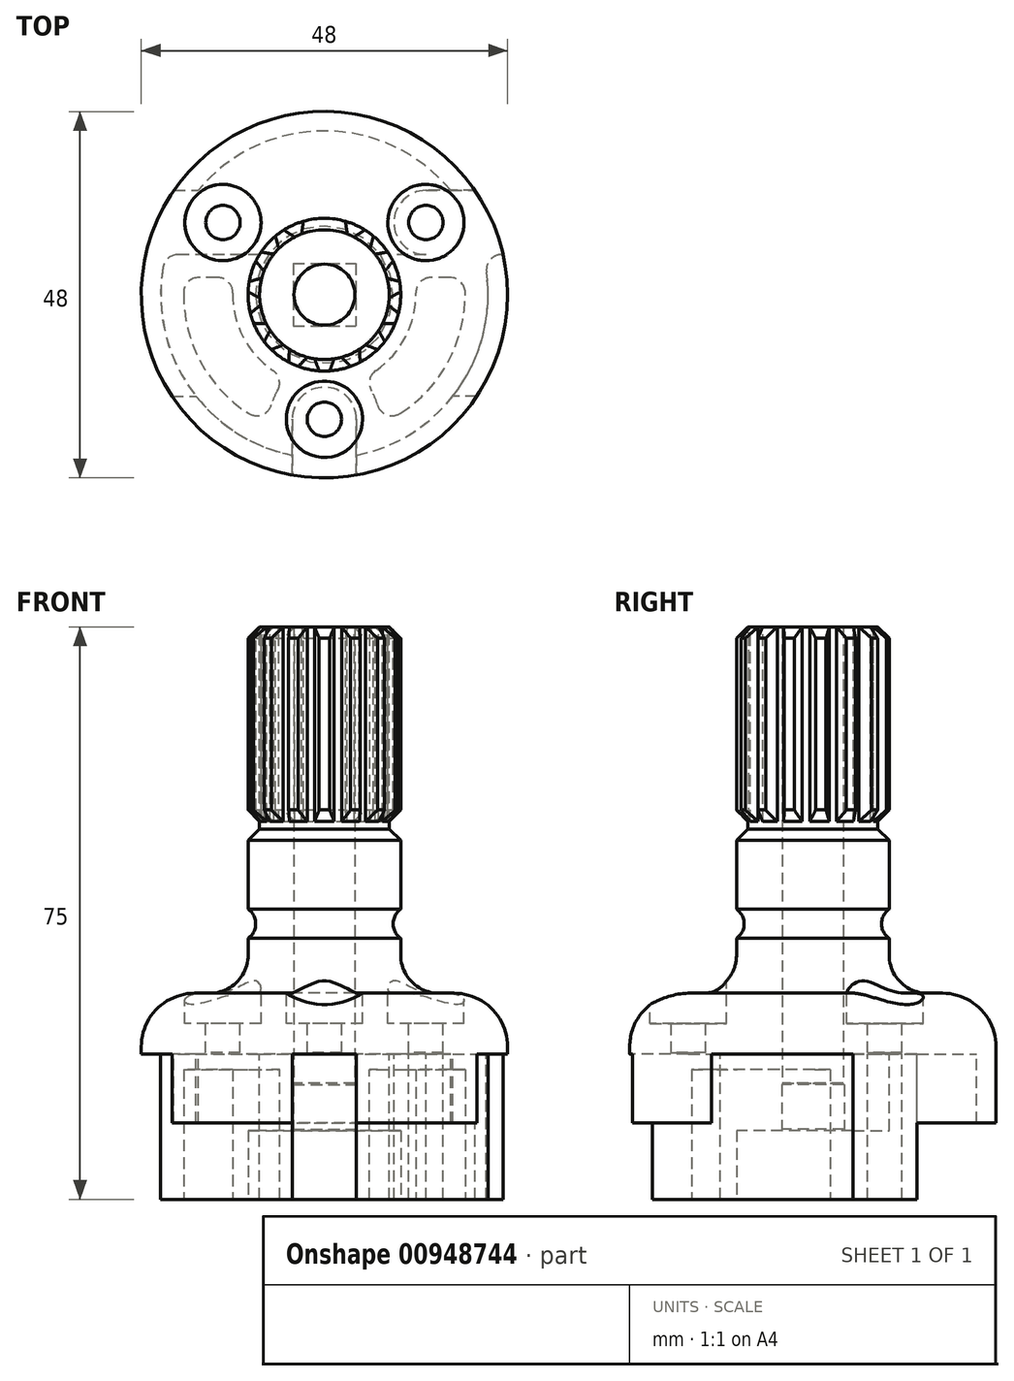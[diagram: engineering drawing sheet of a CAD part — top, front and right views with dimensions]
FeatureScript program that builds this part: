
annotation { "Feature Type Name" : "Feature", "Feature Type Description" : "" }
export const myFeature = defineFeature(function(context is Context, id is Id, definition is map)
    precondition{}
    {
        {
            var Q0;
            Q0=qCreatedBy(makeId("Front.planeOp"),FACE);
            var sketch = newSketch(context, id + "F0", { "sketchPlane" : qUnion([Q0])});
            skLineSegment(sketch, "E0", {"start": v(0, 0) * mm, "end": v(0, 75) * mm});
            skLineSegment(sketch, "E1", {"start": v(24, 0) * mm, "end": v(24, 27) * mm});
            skLineSegment(sketch, "E2", {"start": v(24, 27) * mm, "end": v(10, 27) * mm});
            skLineSegment(sketch, "E3", {"start": v(10, 27) * mm, "end": v(10, 34.2) * mm});
            skLineSegment(sketch, "E4", {"start": v(8.5, 75) * mm, "end": v(0, 75) * mm});
            skArc(sketch, "E5", {"start": v(10, 38) * mm, "mid": v(9, 36.1) * mm, "end": v(10, 34.2) * mm});
            skPoint(sketch, "E6", {"position": v(9, 36.1) * mm});
            skLineSegment(sketch, "E7.trimOffspring", {"start": v(10, 38) * mm, "end": v(10, 47) * mm});
            skLineSegment(sketch, "E8", {"start": v(10, 47) * mm, "end": v(8.5, 48.5) * mm});
            skLineSegment(sketch, "E9", {"start": v(8.5, 48.5) * mm, "end": v(8.5, 49.5) * mm});
            skLineSegment(sketch, "E10", {"start": v(8.5, 49.5) * mm, "end": v(10, 51) * mm});
            skLineSegment(sketch, "E11", {"start": v(8.5, 75) * mm, "end": v(10, 73.5) * mm});
            skPoint(sketch, "E12.orphan", {"position": v(10, 75) * mm});
            skLineSegment(sketch, "E13.trimOffspring", {"start": v(10, 51) * mm, "end": v(10, 73.5) * mm});
            skLineSegment(sketch, "E14", {"start": v(0, 0) * mm, "end": v(24, 0) * mm});
            skSolve(sketch);
        }
        {
            var Q0;
            Q0=makeQuery(id+"F0.imprint","IMPRINT",FACE,{"disambiguationData":[TD([[makeQuery(id+"F0.imprint","IMPRINT",EDGE,{"derivedFrom":sQuery(id+"F0.wireOp",EDGE,"E0")}),-1.0]])]});
            var Q1;
            Q1=sQuery(id+"F0.wireOp",EDGE,"E0");
            revolve(context, id + "F1", {"surfaceOperationType" : NewSurfaceOperationType.NEW, "entities" : qUnion([Q0]), "axis" : qUnion([Q1]), "revolveType" : RevolveType.FULL});
        }
        {
            var Q0;
            Q0=makeQuery(id+"F1.opRevolve","SWEPT_FACE",FACE,{"disambiguationData":[OSD([sQuery(id+"F0.wireOp",EDGE,"E4")])]});
            var sketch = newSketch(context, id + "F2", { "sketchPlane" : qUnion([Q0])});
            skArc(sketch, "E15.0", {"start": v(-4.59, -7.16) * mm, "mid": v(-5, -6.88) * mm, "end": v(-5.39, -6.57) * mm});
            skArc(sketch, "E15.1", {"start": v(4.69, -8.83) * mm, "mid": v(5.88, -8.1) * mm, "end": v(6.95, -7.19) * mm});
            skLineSegment(sketch, "E16", {"start": v(0, 0) * mm, "end": v(0, -10) * mm, "construction": true});
            skLineSegment(sketch, "E17", {"start": v(0.7, -9.98) * mm, "end": v(1.28, -8.4) * mm});
            skLineSegment(sketch, "E18.MirrorCS", {"start": v(-0.7, -9.98) * mm, "end": v(-1.28, -8.4) * mm});
            skLineSegment(sketch, "E19.1.0", {"start": v(4.69, -8.83) * mm, "end": v(4.59, -7.16) * mm});
            skLineSegment(sketch, "E19.1.1", {"start": v(3.43, -9.4) * mm, "end": v(2.25, -8.2) * mm});
            skLineSegment(sketch, "E19.2.0", {"start": v(7.88, -6.16) * mm, "end": v(7.1, -4.67) * mm});
            skLineSegment(sketch, "E19.2.1", {"start": v(6.95, -7.19) * mm, "end": v(5.39, -6.57) * mm});
            skLineSegment(sketch, "E19.3.0", {"start": v(9.7, -2.43) * mm, "end": v(8.39, -1.38) * mm});
            skLineSegment(sketch, "E19.3.1", {"start": v(9.27, -3.74) * mm, "end": v(7.6, -3.81) * mm});
            skLineSegment(sketch, "E19.4.0", {"start": v(9.85, 1.73) * mm, "end": v(8.22, 2.15) * mm});
            skLineSegment(sketch, "E19.4.1", {"start": v(10, 0.36) * mm, "end": v(8.5, -0.4) * mm});
            skLineSegment(sketch, "E19.5.0", {"start": v(8.3, 5.59) * mm, "end": v(6.64, 5.31) * mm});
            skLineSegment(sketch, "E19.5.1", {"start": v(8.99, 4.39) * mm, "end": v(7.92, 3.1) * mm});
            skLineSegment(sketch, "E19.6.0", {"start": v(5.3, 8.48) * mm, "end": v(3.9, 7.55) * mm});
            skLineSegment(sketch, "E19.6.1", {"start": v(6.42, 7.66) * mm, "end": v(5.98, 6.05) * mm});
            skLineSegment(sketch, "E19.7.1", {"start": v(2.75, 9.61) * mm, "end": v(3, 7.95) * mm});
            skLineSegment(sketch, "E19.8.0", {"start": v(-2.75, 9.61) * mm, "end": v(-3, 7.95) * mm});
            skLineSegment(sketch, "E19.9.0", {"start": v(-6.42, 7.66) * mm, "end": v(-5.98, 6.05) * mm});
            skLineSegment(sketch, "E19.9.1", {"start": v(-5.3, 8.48) * mm, "end": v(-3.9, 7.55) * mm});
            skLineSegment(sketch, "E19.10.0", {"start": v(-8.99, 4.39) * mm, "end": v(-7.92, 3.1) * mm});
            skLineSegment(sketch, "E19.10.1", {"start": v(-8.3, 5.59) * mm, "end": v(-6.64, 5.31) * mm});
            skLineSegment(sketch, "E19.11.0", {"start": v(-10, 0.36) * mm, "end": v(-8.5, -0.4) * mm});
            skLineSegment(sketch, "E19.11.1", {"start": v(-9.85, 1.73) * mm, "end": v(-8.22, 2.15) * mm});
            skLineSegment(sketch, "E19.12.0", {"start": v(-9.27, -3.74) * mm, "end": v(-7.6, -3.81) * mm});
            skLineSegment(sketch, "E19.12.1", {"start": v(-9.7, -2.43) * mm, "end": v(-8.39, -1.38) * mm});
            skLineSegment(sketch, "E19.13.0", {"start": v(-6.95, -7.19) * mm, "end": v(-5.39, -6.57) * mm});
            skLineSegment(sketch, "E19.13.1", {"start": v(-7.88, -6.16) * mm, "end": v(-7.1, -4.67) * mm});
            skLineSegment(sketch, "E19.14.0", {"start": v(-3.43, -9.4) * mm, "end": v(-2.25, -8.2) * mm});
            skLineSegment(sketch, "E19.14.1", {"start": v(-4.69, -8.83) * mm, "end": v(-4.59, -7.16) * mm});
            skArc(sketch, "E20.trimOffspring", {"start": v(-7.1, -4.67) * mm, "mid": v(-7.36, -4.25) * mm, "end": v(-7.6, -3.81) * mm});
            skArc(sketch, "E21.trimOffspring", {"start": v(-8.39, -1.38) * mm, "mid": v(-8.45, -0.89) * mm, "end": v(-8.5, -0.4) * mm});
            skArc(sketch, "E22.trimOffspring", {"start": v(-8.22, 2.15) * mm, "mid": v(-8.08, 2.63) * mm, "end": v(-7.92, 3.1) * mm});
            skArc(sketch, "E23.trimOffspring", {"start": v(-6.64, 5.31) * mm, "mid": v(-6.32, 5.69) * mm, "end": v(-5.98, 6.05) * mm});
            skArc(sketch, "E24.trimOffspring", {"start": v(-3.9, 7.55) * mm, "mid": v(-3.46, 7.77) * mm, "end": v(-3, 7.95) * mm});
            skArc(sketch, "E25.trimOffspring", {"start": v(3, 7.95) * mm, "mid": v(3.46, 7.77) * mm, "end": v(3.9, 7.55) * mm});
            skArc(sketch, "E26.trimOffspring", {"start": v(5.98, 6.05) * mm, "mid": v(6.32, 5.69) * mm, "end": v(6.64, 5.31) * mm});
            skArc(sketch, "E27.trimOffspring", {"start": v(7.92, 3.1) * mm, "mid": v(8.08, 2.63) * mm, "end": v(8.22, 2.15) * mm});
            skArc(sketch, "E28.trimOffspring", {"start": v(8.5, -0.4) * mm, "mid": v(8.45, -0.89) * mm, "end": v(8.39, -1.38) * mm});
            skArc(sketch, "E29.trimOffspring", {"start": v(7.6, -3.81) * mm, "mid": v(7.36, -4.25) * mm, "end": v(7.1, -4.67) * mm});
            skArc(sketch, "E30.trimOffspring", {"start": v(5.39, -6.57) * mm, "mid": v(5, -6.88) * mm, "end": v(4.59, -7.16) * mm});
            skArc(sketch, "E31.trimOffspring", {"start": v(2.25, -8.2) * mm, "mid": v(1.77, -8.31) * mm, "end": v(1.28, -8.4) * mm});
            skArc(sketch, "E32.trimOffspring", {"start": v(-1.28, -8.4) * mm, "mid": v(-1.77, -8.31) * mm, "end": v(-2.25, -8.2) * mm});
            skArc(sketch, "E33.trimOffspring", {"start": v(7.88, -6.16) * mm, "mid": v(8.66, -5) * mm, "end": v(9.27, -3.74) * mm});
            skArc(sketch, "E34.trimOffspring", {"start": v(9.7, -2.43) * mm, "mid": v(9.95, -1.05) * mm, "end": v(10, 0.36) * mm});
            skArc(sketch, "E35.trimOffspring", {"start": v(9.85, 1.73) * mm, "mid": v(9.51, 3.1) * mm, "end": v(8.99, 4.39) * mm});
            skArc(sketch, "E36.trimOffspring", {"start": v(8.3, 5.59) * mm, "mid": v(7.43, 6.7) * mm, "end": v(6.42, 7.66) * mm});
            skArc(sketch, "E37.trimOffspring", {"start": v(5.3, 8.48) * mm, "mid": v(4.07, 9.14) * mm, "end": v(2.75, 9.61) * mm});
            skArc(sketch, "E38.trimOffspring", {"start": v(-2.75, 9.61) * mm, "mid": v(-4.07, 9.14) * mm, "end": v(-5.3, 8.48) * mm});
            skArc(sketch, "E39.trimOffspring", {"start": v(-6.42, 7.66) * mm, "mid": v(-7.43, 6.7) * mm, "end": v(-8.3, 5.59) * mm});
            skArc(sketch, "E40.trimOffspring", {"start": v(-8.99, 4.39) * mm, "mid": v(-9.51, 3.1) * mm, "end": v(-9.85, 1.73) * mm});
            skArc(sketch, "E41.trimOffspring", {"start": v(-10, 0.36) * mm, "mid": v(-9.95, -1.05) * mm, "end": v(-9.7, -2.43) * mm});
            skArc(sketch, "E42.trimOffspring", {"start": v(-9.27, -3.74) * mm, "mid": v(-8.66, -5) * mm, "end": v(-7.88, -6.16) * mm});
            skArc(sketch, "E43.trimOffspring", {"start": v(-6.95, -7.19) * mm, "mid": v(-5.88, -8.1) * mm, "end": v(-4.69, -8.83) * mm});
            skArc(sketch, "E44.trimOffspring", {"start": v(-3.43, -9.4) * mm, "mid": v(-2.08, -9.78) * mm, "end": v(-0.7, -9.98) * mm});
            skArc(sketch, "E45.trimOffspring", {"start": v(0.7, -9.98) * mm, "mid": v(2.08, -9.78) * mm, "end": v(3.43, -9.4) * mm});
            skLineSegment(sketch, "E46", {"start": v(0, 0) * mm, "end": v(2.08, -9.78) * mm, "construction": true});
            skSolve(sketch);
        }
        {
            var Q0;
            Q0 = qSketchRegion(id + "F2", true);
            extrude(context, id + "F3", {"entities" : qUnion([Q0]), "operationType" : NewBodyOperationType.REMOVE, "oppositeDirection" : true, "depth" : 26 * mm, "offsetDistance" : 25 * mm});
        }
        {
            var Q0;
            Q0=makeQuery(id+"F1.opRevolve","SWEPT_FACE",FACE,{"disambiguationData":[OSD([sQuery(id+"F0.wireOp",EDGE,"E2")])]});
            var sketch = newSketch(context, id + "F4", { "sketchPlane" : qUnion([Q0])});
            skCircle(sketch, "E47", {"center": v(0, 0) * mm, "radius": 24 * mm});
            skCircle(sketch, "E48", {"center": v(0, 0) * mm, "radius": 21.65 * mm});
            skLineSegment(sketch, "E49", {"start": v(-19.84, 13.5) * mm, "end": v(19.84, 13.5) * mm, "construction": true});
            skLineSegment(sketch, "E50", {"start": v(-19.84, -13.5) * mm, "end": v(19.84, -13.5) * mm, "construction": true});
            skLineSegment(sketch, "E51", {"start": v(-24, 0) * mm, "end": v(24, 0) * mm, "construction": true});
            skLineSegment(sketch, "E52", {"start": v(0, 24) * mm, "end": v(0, -24) * mm, "construction": true});
            skLineSegment(sketch, "E53", {"start": v(-4, -23.66) * mm, "end": v(-4, -21.28) * mm});
            skLineSegment(sketch, "E54.MirrorCS", {"start": v(4, -23.66) * mm, "end": v(4, -21.28) * mm});
            skCircle(sketch, "E55", {"center": v(0, -16.32) * mm, "radius": 4 * mm});
            skCircle(sketch, "E56", {"center": v(0, -16.32) * mm, "radius": 1.9 * mm});
            skCircle(sketch, "E57.1.0", {"center": v(13.3, 9.45) * mm, "radius": 1.9 * mm});
            skCircle(sketch, "E57.1.1", {"center": v(13.3, 9.45) * mm, "radius": 4 * mm});
            skCircle(sketch, "E57.2.0", {"center": v(-13.3, 9.45) * mm, "radius": 1.9 * mm});
            skCircle(sketch, "E57.2.1", {"center": v(-13.3, 9.45) * mm, "radius": 4 * mm});
            skLineSegment(sketch, "E58", {"start": v(-19.84, -13.5) * mm, "end": v(-16.93, -13.5) * mm});
            skLineSegment(sketch, "E59", {"start": v(19.84, -13.5) * mm, "end": v(16.93, -13.5) * mm});
            skLineSegment(sketch, "E60", {"start": v(-19.84, 13.5) * mm, "end": v(-16.93, 13.5) * mm});
            skLineSegment(sketch, "E61", {"start": v(19.84, 13.5) * mm, "end": v(16.93, 13.5) * mm});
            skLineSegment(sketch, "E62", {"start": v(0.5, -21.64) * mm, "end": v(0.5, -20.29) * mm});
            skLineSegment(sketch, "E63.MirrorCS", {"start": v(-0.5, -21.64) * mm, "end": v(-0.5, -20.29) * mm});
            skCircle(sketch, "E64", {"center": v(0, 0) * mm, "radius": 16.32 * mm, "construction": true});
            skLineSegment(sketch, "E65", {"start": v(-13.3, 9.45) * mm, "end": v(13.3, 9.45) * mm, "construction": true});
            skLineSegment(sketch, "E66", {"start": v(0, -16.32) * mm, "end": v(13.3, 9.45) * mm, "construction": true});
            skPoint(sketch, "E67", {"position": v(-11.4, 9.45) * mm});
            skPoint(sketch, "E68", {"position": v(11.4, 9.45) * mm});
            skPoint(sketch, "E69", {"position": v(12.43, 7.76) * mm});
            skPoint(sketch, "E70", {"position": v(0.87, -14.63) * mm});
            skLineSegment(sketch, "E71", {"start": v(0, 0) * mm, "end": v(-17.65, 12.54) * mm, "construction": true});
            skLineSegment(sketch, "E72", {"start": v(-16.25, 12.16) * mm, "end": v(-17.35, 12.95) * mm});
            skLineSegment(sketch, "E73", {"start": v(-16.82, 11.34) * mm, "end": v(-17.93, 12.13) * mm});
            skLineSegment(sketch, "E74.MirrorCS", {"start": v(16.25, 12.16) * mm, "end": v(17.35, 12.95) * mm});
            skLineSegment(sketch, "E75.MirrorCS", {"start": v(16.82, 11.34) * mm, "end": v(17.93, 12.13) * mm});
            skSolve(sketch);
        }
        {
            var Q0;
            Q0=makeQuery(id+"F1.opRevolve","SWEPT_FACE",FACE,{"disambiguationData":[OSD([sQuery(id+"F0.wireOp",EDGE,"E2")])]});
            var sketch = newSketch(context, id + "F5", { "sketchPlane" : qUnion([Q0])});
            skCircle(sketch, "E76.0", {"center": v(0, 0) * mm, "radius": 24 * mm, "construction": true});
            skCircle(sketch, "E77.0", {"center": v(-13.3, 9.45) * mm, "radius": 4 * mm, "construction": true});
            skLineSegment(sketch, "E77.1", {"start": v(-19.84, 13.5) * mm, "end": v(19.84, 13.5) * mm, "construction": true});
            skCircle(sketch, "E78.0", {"center": v(0, 0) * mm, "radius": 21.65 * mm, "construction": true});
            skCircle(sketch, "E79.0", {"center": v(0, -16.32) * mm, "radius": 4 * mm, "construction": true});
            skLineSegment(sketch, "E79.1", {"start": v(-4, -23.66) * mm, "end": v(-4, -21.28) * mm, "construction": true});
            skLineSegment(sketch, "E79.2", {"start": v(4, -23.66) * mm, "end": v(4, -21.28) * mm, "construction": true});
            skArc(sketch, "E80", {"start": v(-13.3, 5.25) * mm, "mid": v(-9.1, 9.45) * mm, "end": v(-13.3, 13.65) * mm});
            skLineSegment(sketch, "E81.0", {"start": v(-19.84, -13.5) * mm, "end": v(19.84, -13.5) * mm, "construction": true});
            skLineSegment(sketch, "E82", {"start": v(-16.83, -13.3) * mm, "end": v(-19.98, -13.3) * mm});
            skArc(sketch, "E83", {"start": v(0, 24) * mm, "mid": v(-21.16, 11.33) * mm, "end": v(-19.98, -13.3) * mm});
            skArc(sketch, "E84", {"start": v(-23.42, 5.25) * mm, "mid": v(-18.74, -15) * mm, "end": v(0, -24) * mm});
            skLineSegment(sketch, "E85", {"start": v(0, -24) * mm, "end": v(0, 24) * mm, "construction": true});
            skArc(sketch, "E86.MirrorCS", {"start": v(0, 24) * mm, "mid": v(21.16, 11.33) * mm, "end": v(19.98, -13.3) * mm});
            skLineSegment(sketch, "E87.MirrorCS", {"start": v(16.83, -13.3) * mm, "end": v(19.98, -13.3) * mm});
            skArc(sketch, "E88.MirrorCS", {"start": v(23.42, 5.25) * mm, "mid": v(18.74, -15) * mm, "end": v(0, -24) * mm});
            skArc(sketch, "E89.MirrorCS", {"start": v(13.3, 5.25) * mm, "mid": v(9.1, 9.45) * mm, "end": v(13.3, 13.65) * mm});
            skCircle(sketch, "E90", {"center": v(0, 0) * mm, "radius": 4 * mm});
            skCircle(sketch, "E91", {"center": v(13.3, 9.45) * mm, "radius": 2.25 * mm});
            skCircle(sketch, "E92", {"center": v(-13.3, 9.45) * mm, "radius": 2.25 * mm});
            skCircle(sketch, "E93", {"center": v(0, -16.32) * mm, "radius": 2.25 * mm});
            skArc(sketch, "E94", {"start": v(4.2, -16.32) * mm, "mid": v(0, -12.12) * mm, "end": v(-4.2, -16.32) * mm});
            skLineSegment(sketch, "E95", {"start": v(4.2, -16.32) * mm, "end": v(4.2, -23.66) * mm});
            skLineSegment(sketch, "E96", {"start": v(-4.2, -16.32) * mm, "end": v(-4.2, -23.63) * mm});
            skLineSegment(sketch, "E97", {"start": v(-23.42, 5.25) * mm, "end": v(23.42, 5.25) * mm});
            skArc(sketch, "E98", {"start": v(16.54, 13.65) * mm, "mid": v(0, 21.45) * mm, "end": v(-16.54, 13.65) * mm});
            skLineSegment(sketch, "E99", {"start": v(13.3, 13.65) * mm, "end": v(19.74, 13.65) * mm});
            skLineSegment(sketch, "E100", {"start": v(-13.3, 13.65) * mm, "end": v(-19.74, 13.65) * mm});
            skArc(sketch, "E101", {"start": v(16.83, -13.3) * mm, "mid": v(20.98, -4.49) * mm, "end": v(20.8, 5.25) * mm});
            skArc(sketch, "E102.MirrorCS", {"start": v(-16.83, -13.3) * mm, "mid": v(-20.98, -4.49) * mm, "end": v(-20.8, 5.25) * mm});
            skArc(sketch, "E103", {"start": v(4.2, -21.03) * mm, "mid": v(11.2, -18.3) * mm, "end": v(16.83, -13.3) * mm});
            skArc(sketch, "E104.MirrorCS", {"start": v(-4.2, -21.03) * mm, "mid": v(-11.2, -18.3) * mm, "end": v(-16.83, -13.3) * mm});
            skSolve(sketch);
        }
        {
            var Q0;
            Q0=makeQuery(id+"F5.imprint","IMPRINT",FACE,{"disambiguationData":[TD([[makeQuery(id+"F5.imprint","IMPRINT",EDGE,{"derivedFrom":sQuery(id+"F5.wireOp",EDGE,"E93")}),-1.0]])]});
            var Q1;
            {var subQ0=sQuery(id+"F5.wireOp",EDGE,"E80");Q1=makeQuery(id+"F5.imprint","IMPRINT",FACE,{"disambiguationData":[TD([[makeQuery(id+"F5.imprint","IMPRINT",EDGE,{"derivedFrom":subQ0}),1.0]])]});}
            var Q2;
            Q2=makeQuery(id+"F5.imprint","IMPRINT",FACE,{"disambiguationData":[TD([[makeQuery(id+"F5.imprint","IMPRINT",EDGE,{"derivedFrom":sQuery(id+"F5.wireOp",EDGE,"E92")}),1.0]])]});
            var Q3;
            Q3=makeQuery(id+"F5.imprint","IMPRINT",FACE,{"disambiguationData":[TD([[makeQuery(id+"F5.imprint","IMPRINT",EDGE,{"derivedFrom":sQuery(id+"F5.wireOp",EDGE,"E91")}),1.0]])]});
            var Q4;
            Q4=makeQuery(id+"F5.imprint","IMPRINT",FACE,{"disambiguationData":[TD([[makeQuery(id+"F5.imprint","IMPRINT",EDGE,{"derivedFrom":sQuery(id+"F5.wireOp",EDGE,"E93")}),1.0]])]});
            var Q5;
            {var subQ1=sQuery(id+"F5.wireOp",EDGE,"E89.MirrorCS");Q5=makeQuery(id+"F5.imprint","IMPRINT",FACE,{"disambiguationData":[TD([[makeQuery(id+"F5.imprint","IMPRINT",EDGE,{"derivedFrom":subQ1}),-1.0]])]});}
            var Q6;
            {var subQ0=sQuery(id+"F5.wireOp",EDGE,"E82");Q6=makeQuery(id+"F5.imprint","IMPRINT",FACE,{"disambiguationData":[TD([[makeQuery(id+"F5.imprint","IMPRINT",EDGE,{"derivedFrom":subQ0}),-1.0]])]});}
            var Q7;
            {var subQ0=sQuery(id+"F5.wireOp",EDGE,"E87.MirrorCS");Q7=makeQuery(id+"F5.imprint","IMPRINT",FACE,{"disambiguationData":[TD([[makeQuery(id+"F5.imprint","IMPRINT",EDGE,{"derivedFrom":subQ0}),1.0]])]});}
            extrude(context, id + "F6", {"entities" : qUnion([Q0, Q1, Q2, Q3, Q4, Q5, Q6, Q7]), "operationType" : NewBodyOperationType.REMOVE, "endBound" : BoundingType.THROUGH_ALL, "oppositeDirection" : true, "depth" : (25 + 9) * mm, "offsetDistance" : 25 * mm, "hasSecondDirection" : true, "secondDirectionOppositeDirection" : true, "secondDirectionDepth" : 8 * mm});
        }
        {
            var Q0;
            {var subQ1=sQuery(id+"F5.wireOp",EDGE,"E98");Q0=makeQuery(id+"F5.imprint","IMPRINT",FACE,{"disambiguationData":[TD([[makeQuery(id+"F5.imprint","IMPRINT",EDGE,{"derivedFrom":subQ1}),-1.0]])]});}
            var Q1;
            {var subQ5=sQuery(id+"F5.wireOp",EDGE,"E80");Q1=makeQuery(id+"F5.imprint","IMPRINT",FACE,{"disambiguationData":[TD([[makeQuery(id+"F5.imprint","IMPRINT",EDGE,{"derivedFrom":subQ5}),1.0]])]});}
            var Q2;
            Q2=makeQuery(id+"F5.imprint","IMPRINT",FACE,{"disambiguationData":[TD([[makeQuery(id+"F5.imprint","IMPRINT",EDGE,{"derivedFrom":sQuery(id+"F5.wireOp",EDGE,"E92")}),1.0]])]});
            var Q3;
            {var subQ0=sQuery(id+"F5.wireOp",EDGE,"E82");Q3=makeQuery(id+"F5.imprint","IMPRINT",FACE,{"disambiguationData":[TD([[makeQuery(id+"F5.imprint","IMPRINT",EDGE,{"derivedFrom":subQ0}),-1.0]])]});}
            var Q4;
            {var subQ0=sQuery(id+"F5.wireOp",EDGE,"E87.MirrorCS");Q4=makeQuery(id+"F5.imprint","IMPRINT",FACE,{"disambiguationData":[TD([[makeQuery(id+"F5.imprint","IMPRINT",EDGE,{"derivedFrom":subQ0}),1.0]])]});}
            var Q5;
            {var subQ1=sQuery(id+"F5.wireOp",EDGE,"E89.MirrorCS");Q5=makeQuery(id+"F5.imprint","IMPRINT",FACE,{"disambiguationData":[TD([[makeQuery(id+"F5.imprint","IMPRINT",EDGE,{"derivedFrom":subQ1}),-1.0]])]});}
            var Q6;
            Q6=makeQuery(id+"F5.imprint","IMPRINT",FACE,{"disambiguationData":[TD([[makeQuery(id+"F5.imprint","IMPRINT",EDGE,{"derivedFrom":sQuery(id+"F5.wireOp",EDGE,"E91")}),1.0]])]});
            var Q7;
            Q7=makeQuery(id+"F5.imprint","IMPRINT",FACE,{"disambiguationData":[TD([[makeQuery(id+"F5.imprint","IMPRINT",EDGE,{"derivedFrom":sQuery(id+"F5.wireOp",EDGE,"E93")}),-1.0]])]});
            var Q8;
            Q8=makeQuery(id+"F5.imprint","IMPRINT",FACE,{"disambiguationData":[TD([[makeQuery(id+"F5.imprint","IMPRINT",EDGE,{"derivedFrom":sQuery(id+"F5.wireOp",EDGE,"E93")}),1.0]])]});
            var Q9;
            {var subQ0=sQuery(id+"F5.wireOp",EDGE,"E87.MirrorCS");Q9=makeQuery(id+"F5.imprint","IMPRINT",FACE,{"disambiguationData":[TD([[makeQuery(id+"F5.imprint","IMPRINT",EDGE,{"derivedFrom":subQ0}),-1.0]])]});}
            var Q10;
            {var subQ0=sQuery(id+"F5.wireOp",EDGE,"E82");Q10=makeQuery(id+"F5.imprint","IMPRINT",FACE,{"disambiguationData":[TD([[makeQuery(id+"F5.imprint","IMPRINT",EDGE,{"derivedFrom":subQ0}),1.0]])]});}
            extrude(context, id + "F7", {"entities" : qUnion([Q0, Q1, Q2, Q3, Q4, Q5, Q6, Q7, Q8, Q9, Q10]), "operationType" : NewBodyOperationType.REMOVE, "endBound" : BoundingType.THROUGH_ALL, "oppositeDirection" : true, "depth" : 25 * mm, "offsetDistance" : 25 * mm, "hasSecondDirection" : true, "secondDirectionOppositeDirection" : true, "secondDirectionDepth" : (9 + 8) * mm});
        }
        {
            var Q0;
            Q0=makeQuery(id+"F1.opRevolve","SWEPT_EDGE",EDGE,{"disambiguationData":[OSD([sQuery(id+"F0.wireOp",EDGE,"E2"),sQuery(id+"F0.wireOp",EDGE,"E3")])]});
            fillet(context, id + "F8", {"entities" : qUnion([Q0]), "radius" : 5 * mm, "tangentPropagation" : true, "allowEdgeOverflow" : false});
        }
        {
            var Q0;
            Q0=makeQuery(id+"F1.opRevolve","SWEPT_EDGE",EDGE,{"disambiguationData":[OSD([sQuery(id+"F0.wireOp",EDGE,"E1"),sQuery(id+"F0.wireOp",EDGE,"E2")])]});
            fillet(context, id + "F9", {"entities" : qUnion([Q0]), "radius" : 7 * mm, "tangentPropagation" : true, "allowEdgeOverflow" : false});
        }
        {
            var Q0;
            Q0=makeQuery(id+"F5.imprint","IMPRINT",FACE,{"disambiguationData":[TD([[makeQuery(id+"F5.imprint","IMPRINT",EDGE,{"derivedFrom":sQuery(id+"F5.wireOp",EDGE,"E91")}),1.0]])]});
            var Q1;
            Q1=makeQuery(id+"F5.imprint","IMPRINT",FACE,{"disambiguationData":[TD([[makeQuery(id+"F5.imprint","IMPRINT",EDGE,{"derivedFrom":sQuery(id+"F5.wireOp",EDGE,"E93")}),1.0]])]});
            var Q2;
            Q2=makeQuery(id+"F5.imprint","IMPRINT",FACE,{"disambiguationData":[TD([[makeQuery(id+"F5.imprint","IMPRINT",EDGE,{"derivedFrom":sQuery(id+"F5.wireOp",EDGE,"E92")}),1.0]])]});
            var Q3;
            Q3=makeQuery(id+"F6.boolean.opBoolean","COPY",FACE,{"derivedFrom":makeQuery(id+"F6.opExtrude","CAP_FACE",FACE,{"disambiguationData":[OSD([sQuery(id+"F5.wireOp",EDGE,"E86.MirrorCS"),sQuery(id+"F5.wireOp",EDGE,"E87.MirrorCS"),sQuery(id+"F5.wireOp",EDGE,"E88.MirrorCS"),sQuery(id+"F5.wireOp",EDGE,"E89.MirrorCS"),sQuery(id+"F5.wireOp",EDGE,"E97"),sQuery(id+"F5.wireOp",EDGE,"E99"),sQuery(id+"F5.wireOp",EDGE,"E101")])],"isStart":true})});
            extrude(context, id + "F10", {"entities" : qUnion([Q0, Q1, Q2]), "operationType" : NewBodyOperationType.REMOVE, "endBound" : BoundingType.UP_TO_SURFACE, "oppositeDirection" : true, "depth" : 25 * mm, "endBoundEntityFace" : qUnion([Q3]), "hasOffset" : true, "offsetDistance" : 0.2 * mm});
        }
        {
            var Q0;
            Q0=makeQuery(id+"F1.opRevolve","SWEPT_FACE",FACE,{"disambiguationData":[OSD([sQuery(id+"F0.wireOp",EDGE,"E2")])]});
            var sketch = newSketch(context, id + "F11", { "sketchPlane" : qUnion([Q0])});
            skCircle(sketch, "E105", {"center": v(13.3, 9.45) * mm, "radius": 5 * mm});
            skCircle(sketch, "E106", {"center": v(0, -16.32) * mm, "radius": 5 * mm});
            skCircle(sketch, "E107", {"center": v(-13.3, 9.45) * mm, "radius": 5 * mm});
            skSolve(sketch);
        }
        {
            var Q0;
            Q0 = qSketchRegion(id + "F11", true);
            extrude(context, id + "F12", {"entities" : qUnion([Q0]), "operationType" : NewBodyOperationType.REMOVE, "oppositeDirection" : true, "depth" : 4 * mm, "offsetDistance" : 25 * mm, "hasSecondDirection" : true, "secondDirectionBound" : SecondDirectionBoundingType.THROUGH_ALL, "secondDirectionOppositeDirection" : false, "secondDirectionDepth" : 25 * mm});
        }
        {
            var Q0;
            Q0=makeQuery(id+"F1.opRevolve","SWEPT_FACE",FACE,{"disambiguationData":[OSD([sQuery(id+"F0.wireOp",EDGE,"E14")])]});
            var sketch = newSketch(context, id + "F13", { "sketchPlane" : qUnion([Q0])});
            skCircle(sketch, "E108", {"center": v(0, 0) * mm, "radius": 4 * mm});
            skSolve(sketch);
        }
        {
            var Q0;
            Q0=makeQuery(id+"F6.boolean.opBoolean","COPY",EDGE,{"derivedFrom":makeQuery(id+"F6.opExtrude","SWEPT_EDGE",EDGE,{"disambiguationData":[OSD([sQuery(id+"F5.wireOp",EDGE,"E97"),sQuery(id+"F5.wireOp",EDGE,"E102.MirrorCS")])]})});
            var Q1;
            Q1=makeQuery(id+"F7.boolean.opBoolean","COPY",EDGE,{"derivedFrom":makeQuery(id+"F7.opExtrude","SWEPT_EDGE",EDGE,{"disambiguationData":[OSD([sQuery(id+"F5.wireOp",EDGE,"E98"),sQuery(id+"F5.wireOp",EDGE,"E100")])]})});
            var Q2;
            Q2=makeQuery(id+"F7.boolean.opBoolean","COPY",EDGE,{"derivedFrom":makeQuery(id+"F7.opExtrude","SWEPT_EDGE",EDGE,{"disambiguationData":[OSD([sQuery(id+"F5.wireOp",EDGE,"E98"),sQuery(id+"F5.wireOp",EDGE,"E99")])]})});
            var Q3;
            Q3=makeQuery(id+"F6.boolean.opBoolean","COPY",EDGE,{"derivedFrom":makeQuery(id+"F6.opExtrude","SWEPT_EDGE",EDGE,{"disambiguationData":[OSD([sQuery(id+"F5.wireOp",EDGE,"E97"),sQuery(id+"F5.wireOp",EDGE,"E101")])]})});
            var Q4;
            Q4=makeQuery(id+"F7.boolean.opBoolean","COPY",EDGE,{"derivedFrom":makeQuery(id+"F7.opExtrude","SWEPT_EDGE",EDGE,{"disambiguationData":[OSD([sQuery(id+"F5.wireOp",EDGE,"E95"),sQuery(id+"F5.wireOp",EDGE,"E103")])]})});
            var Q5;
            Q5=makeQuery(id+"F7.boolean.opBoolean","COPY",EDGE,{"derivedFrom":makeQuery(id+"F7.opExtrude","SWEPT_EDGE",EDGE,{"disambiguationData":[OSD([sQuery(id+"F5.wireOp",EDGE,"E96"),sQuery(id+"F5.wireOp",EDGE,"E104.MirrorCS")])]})});
            fillet(context, id + "F14", {"entities" : qUnion([Q0, Q1, Q2, Q3, Q4, Q5]), "radius" : 2 * mm, "tangentPropagation" : true, "allowEdgeOverflow" : false});
        }
        {
            var Q0;
            Q0=makeQuery(id+"F1.opRevolve","SWEPT_FACE",FACE,{"disambiguationData":[OSD([sQuery(id+"F0.wireOp",EDGE,"E14")])]});
            var sketch = newSketch(context, id + "F15", { "sketchPlane" : qUnion([Q0])});
            skLineSegment(sketch, "E109.bottom", {"start": v(-4.1, -4.1) * mm, "end": v(4.1, -4.1) * mm});
            skLineSegment(sketch, "E109.top", {"start": v(-4.1, 4.1) * mm, "end": v(4.1, 4.1) * mm});
            skLineSegment(sketch, "E109.left", {"start": v(-4.1, -4.1) * mm, "end": v(-4.1, 4.1) * mm});
            skLineSegment(sketch, "E109.right", {"start": v(4.1, -4.1) * mm, "end": v(4.1, 4.1) * mm});
            skPoint(sketch, "E109.middle", {"position": v(0, 0) * mm});
            skCircle(sketch, "E110", {"center": v(0, 0) * mm, "radius": 10 * mm});
            skSolve(sketch);
        }
        {
            var Q0;
            Q0=makeQuery(id+"F15.imprint","IMPRINT",FACE,{"disambiguationData":[TD([[makeQuery(id+"F15.imprint","IMPRINT",EDGE,{"derivedFrom":sQuery(id+"F15.wireOp",EDGE,"E109.bottom")}),-1.0]])]});
            var Q1;
            Q1=makeQuery(id+"F15.imprint","IMPRINT",FACE,{"disambiguationData":[TD([[makeQuery(id+"F15.imprint","IMPRINT",EDGE,{"derivedFrom":sQuery(id+"F15.wireOp",EDGE,"E109.bottom")}),1.0]])]});
            var Q2;
            Q2=makeQuery(id+"F1.opRevolve","SWEPT_FACE",FACE,{"disambiguationData":[OSD([sQuery(id+"F0.wireOp",EDGE,"E4")])]});
            extrude(context, id + "F16", {"entities" : qUnion([Q0, Q1]), "operationType" : NewBodyOperationType.REMOVE, "endBound" : BoundingType.UP_TO_SURFACE, "oppositeDirection" : true, "depth" : 25 * mm, "endBoundEntityFace" : qUnion([Q2]), "hasOffset" : true, "offsetDistance" : (75 - 9) * mm});
        }
        {
            var Q0;
            Q0=makeQuery(id+"F15.imprint","IMPRINT",FACE,{"disambiguationData":[TD([[makeQuery(id+"F15.imprint","IMPRINT",EDGE,{"derivedFrom":sQuery(id+"F15.wireOp",EDGE,"E109.bottom")}),1.0]])]});
            var Q1;
            Q1=makeQuery(id+"F16.boolean.opBoolean","COPY",FACE,{"derivedFrom":makeQuery(id+"F16.opExtrude","CAP_FACE",FACE,{"disambiguationData":[OSD([sQuery(id+"F15.wireOp",EDGE,"E110")])],"isStart":false})});
            var Q2;
            Q2=makeQuery(id+"F16.boolean.opBoolean","COPY",FACE,{"derivedFrom":makeQuery(id+"F16.opExtrude","CAP_FACE",FACE,{"disambiguationData":[OSD([sQuery(id+"F15.wireOp",EDGE,"E110")])],"isStart":false})});
            extrude(context, id + "F17", {"entities" : qUnion([Q0]), "operationType" : NewBodyOperationType.REMOVE, "endBound" : BoundingType.UP_TO_SURFACE, "oppositeDirection" : true, "depth" : 8 * mm, "endBoundEntityFace" : qUnion([Q1]), "hasOffset" : true, "offsetDistance" : 6 * mm, "offsetOppositeDirection" : true, "hasSecondDirection" : true, "secondDirectionBound" : SecondDirectionBoundingType.UP_TO_SURFACE, "secondDirectionOppositeDirection" : true, "secondDirectionDepth" : 25 * mm, "secondDirectionBoundEntityFace" : qUnion([Q2]), "hasSecondDirectionOffset" : true, "secondDirectionOffsetDistance" : 0.2 * mm, "secondDirectionOffsetOppositeDirection" : true});
        }
        {
            var Q0;
            Q0=makeQuery(id+"F13.imprint","IMPRINT",FACE,{"disambiguationData":[TD([[makeQuery(id+"F13.imprint","IMPRINT",EDGE,{"derivedFrom":sQuery(id+"F13.wireOp",EDGE,"E108")}),1.0]])]});
            var Q1;
            Q1=makeQuery(id+"F13.imprint","IMPRINT",FACE,{"disambiguationData":[TD([[makeQuery(id+"F13.imprint","IMPRINT",EDGE,{"derivedFrom":sQuery(id+"F13.wireOp",EDGE,"1cwd8fAG-wdHr-gfUo-fLdx-JzWl2PM3jYLh")}),1.0]])]});
            var Q2;
            Q2=makeQuery(id+"F17.boolean.opBoolean","COPY",FACE,{"derivedFrom":makeQuery(id+"F17.opExtrude","CAP_FACE",FACE,{"disambiguationData":[OSD([sQuery(id+"F15.wireOp",EDGE,"E109.bottom"),sQuery(id+"F15.wireOp",EDGE,"E109.top"),sQuery(id+"F15.wireOp",EDGE,"E109.left"),sQuery(id+"F15.wireOp",EDGE,"E109.right")])],"isStart":false})});
            extrude(context, id + "F18", {"entities" : qUnion([Q0, Q1]), "operationType" : NewBodyOperationType.REMOVE, "endBound" : BoundingType.THROUGH_ALL, "oppositeDirection" : true, "depth" : 25 * mm, "hasOffset" : true, "offsetDistance" : 25 * mm, "hasSecondDirection" : true, "secondDirectionBound" : SecondDirectionBoundingType.UP_TO_SURFACE, "secondDirectionOppositeDirection" : true, "secondDirectionDepth" : 25 * mm, "secondDirectionBoundEntityFace" : qUnion([Q2]), "hasSecondDirectionOffset" : true, "secondDirectionOffsetDistance" : 0.2 * mm, "secondDirectionOffsetOppositeDirection" : true});
        }
        {
            var Q0;
            Q0=makeQuery(id+"F13.imprint","IMPRINT",FACE,{"disambiguationData":[TD([[makeQuery(id+"F13.imprint","IMPRINT",EDGE,{"derivedFrom":sQuery(id+"F13.wireOp",EDGE,"E108")}),-1.0]])]});
            var sketch = newSketch(context, id + "F19", { "sketchPlane" : qUnion([Q0])});
            skLineSegment(sketch, "E111.0", {"start": v(18.31, -2.25) * mm, "end": v(13.3, -2.25) * mm});
            skArc(sketch, "E111.1", {"start": v(9.7, -15.7) * mm, "mid": v(7.3, -13.42) * mm, "end": v(6.15, -10.3) * mm});
            skArc(sketch, "E111.2", {"start": v(18.31, -2.25) * mm, "mid": v(15.98, 9.23) * mm, "end": v(7.2, 16.99) * mm});
            skArc(sketch, "E111.3", {"start": v(-9.7, -15.7) * mm, "mid": v(0, -18.45) * mm, "end": v(9.7, -15.7) * mm});
            skArc(sketch, "E111.4", {"start": v(-9.7, -15.7) * mm, "mid": v(-7.3, -13.42) * mm, "end": v(-6.15, -10.3) * mm});
            skLineSegment(sketch, "E111.5", {"start": v(-13.3, -2.25) * mm, "end": v(-18.31, -2.25) * mm});
            skLineSegment(sketch, "E111.6", {"start": v(7.2, 16.99) * mm, "end": v(7.2, 16.32) * mm});
            skArc(sketch, "E111.7", {"start": v(-7.2, 16.32) * mm, "mid": v(-6.58, 13.4) * mm, "end": v(-4.84, 10.98) * mm});
            skLineSegment(sketch, "E111.8", {"start": v(-7.2, 16.99) * mm, "end": v(-7.2, 16.32) * mm});
            skArc(sketch, "E111.9", {"start": v(-18.31, -2.25) * mm, "mid": v(-15.98, 9.23) * mm, "end": v(-7.2, 16.99) * mm});
            skArc(sketch, "E112", {"start": v(11.75, -2.42) * mm, "mid": v(10.66, 5.5) * mm, "end": v(4.84, 10.98) * mm});
            skArc(sketch, "E113.trimOffspring", {"start": v(11.75, -2.42) * mm, "mid": v(12.52, -2.3) * mm, "end": v(13.3, -2.25) * mm});
            skArc(sketch, "E114.trimOffspring", {"start": v(4.84, 10.98) * mm, "mid": v(6.58, 13.4) * mm, "end": v(7.2, 16.32) * mm});
            skArc(sketch, "E115.trimOffspring", {"start": v(-4.84, 10.98) * mm, "mid": v(-10.66, 5.5) * mm, "end": v(-11.75, -2.42) * mm});
            skArc(sketch, "E116.trimOffspring", {"start": v(-11.75, -2.42) * mm, "mid": v(-12.52, -2.3) * mm, "end": v(-13.3, -2.25) * mm});
            skArc(sketch, "E117.trimOffspring", {"start": v(-6.15, -10.3) * mm, "mid": v(0, -12) * mm, "end": v(6.15, -10.3) * mm});
            skSolve(sketch);
        }
        {
            var Q0;
            Q0 = qSketchRegion(id + "F19", true);
            var Q1;
            Q1=makeQuery(id+"F6.boolean.opBoolean","COPY",FACE,{"derivedFrom":makeQuery(id+"F6.opExtrude","CAP_FACE",FACE,{"disambiguationData":[OSD([sQuery(id+"F5.wireOp",EDGE,"E86.MirrorCS"),sQuery(id+"F5.wireOp",EDGE,"E87.MirrorCS"),sQuery(id+"F5.wireOp",EDGE,"E88.MirrorCS"),sQuery(id+"F5.wireOp",EDGE,"E89.MirrorCS"),sQuery(id+"F5.wireOp",EDGE,"E97"),sQuery(id+"F5.wireOp",EDGE,"E99"),sQuery(id+"F5.wireOp",EDGE,"E101")])],"isStart":true})});
            var Q2;
            Q2=makeQuery(id+"F1.opRevolve","SWEPT_BODY",BODY,{"disambiguationData":[OSD([sQuery(id+"F0.wireOp",EDGE,"E0"),sQuery(id+"F0.wireOp",EDGE,"E1"),sQuery(id+"F0.wireOp",EDGE,"E2"),sQuery(id+"F0.wireOp",EDGE,"E3"),sQuery(id+"F0.wireOp",EDGE,"E4"),sQuery(id+"F0.wireOp",EDGE,"E5"),sQuery(id+"F0.wireOp",EDGE,"E7.trimOffspring"),sQuery(id+"F0.wireOp",EDGE,"E8"),sQuery(id+"F0.wireOp",EDGE,"E9"),sQuery(id+"F0.wireOp",EDGE,"E10"),sQuery(id+"F0.wireOp",EDGE,"E11"),sQuery(id+"F0.wireOp",EDGE,"E13.trimOffspring"),sQuery(id+"F0.wireOp",EDGE,"E14")])]});
            extrude(context, id + "F20", {"entities" : qUnion([Q0]), "operationType" : NewBodyOperationType.REMOVE, "endBound" : BoundingType.UP_TO_SURFACE, "oppositeDirection" : true, "depth" : 20 * mm, "endBoundEntityFace" : qUnion([Q1]), "endBoundEntityBody" : qUnion([Q2]), "hasOffset" : true, "offsetDistance" : 2 * mm});
        }
        {
            var Q0;
            Q0=makeQuery(id+"F20.boolean.opBoolean","COPY",EDGE,{"derivedFrom":makeQuery(id+"F20.opExtrude","SWEPT_EDGE",EDGE,{"disambiguationData":[OSD([sQuery(id+"F19.wireOp",EDGE,"E111.8"),sQuery(id+"F19.wireOp",EDGE,"E111.9")])]})});
            var Q1;
            Q1=makeQuery(id+"F20.boolean.opBoolean","COPY",EDGE,{"derivedFrom":makeQuery(id+"F20.opExtrude","SWEPT_EDGE",EDGE,{"disambiguationData":[OSD([sQuery(id+"F19.wireOp",EDGE,"E111.7"),sQuery(id+"F19.wireOp",EDGE,"E115.trimOffspring")])]})});
            var Q2;
            Q2=makeQuery(id+"F20.boolean.opBoolean","COPY",EDGE,{"derivedFrom":makeQuery(id+"F20.opExtrude","SWEPT_EDGE",EDGE,{"disambiguationData":[OSD([sQuery(id+"F19.wireOp",EDGE,"E115.trimOffspring"),sQuery(id+"F19.wireOp",EDGE,"E116.trimOffspring")])]})});
            var Q3;
            Q3=makeQuery(id+"F20.boolean.opBoolean","COPY",EDGE,{"derivedFrom":makeQuery(id+"F20.opExtrude","SWEPT_EDGE",EDGE,{"disambiguationData":[OSD([sQuery(id+"F19.wireOp",EDGE,"E111.5"),sQuery(id+"F19.wireOp",EDGE,"E111.9")])]})});
            var Q4;
            Q4=makeQuery(id+"F20.boolean.opBoolean","COPY",EDGE,{"derivedFrom":makeQuery(id+"F20.opExtrude","SWEPT_EDGE",EDGE,{"disambiguationData":[OSD([sQuery(id+"F19.wireOp",EDGE,"E111.2"),sQuery(id+"F19.wireOp",EDGE,"E111.6")])]})});
            var Q5;
            Q5=makeQuery(id+"F20.boolean.opBoolean","COPY",EDGE,{"derivedFrom":makeQuery(id+"F20.opExtrude","SWEPT_EDGE",EDGE,{"disambiguationData":[OSD([sQuery(id+"F19.wireOp",EDGE,"E112"),sQuery(id+"F19.wireOp",EDGE,"E114.trimOffspring")])]})});
            var Q6;
            Q6=makeQuery(id+"F20.boolean.opBoolean","COPY",EDGE,{"derivedFrom":makeQuery(id+"F20.opExtrude","SWEPT_EDGE",EDGE,{"disambiguationData":[OSD([sQuery(id+"F19.wireOp",EDGE,"E112"),sQuery(id+"F19.wireOp",EDGE,"E113.trimOffspring")])]})});
            var Q7;
            Q7=makeQuery(id+"F20.boolean.opBoolean","COPY",EDGE,{"derivedFrom":makeQuery(id+"F20.opExtrude","SWEPT_EDGE",EDGE,{"disambiguationData":[OSD([sQuery(id+"F19.wireOp",EDGE,"E111.0"),sQuery(id+"F19.wireOp",EDGE,"E111.2")])]})});
            var Q8;
            Q8=makeQuery(id+"F20.boolean.opBoolean","COPY",EDGE,{"derivedFrom":makeQuery(id+"F20.opExtrude","SWEPT_EDGE",EDGE,{"disambiguationData":[OSD([sQuery(id+"F19.wireOp",EDGE,"E111.1"),sQuery(id+"F19.wireOp",EDGE,"E117.trimOffspring")])]})});
            var Q9;
            Q9=makeQuery(id+"F20.boolean.opBoolean","COPY",EDGE,{"derivedFrom":makeQuery(id+"F20.opExtrude","SWEPT_EDGE",EDGE,{"disambiguationData":[OSD([sQuery(id+"F19.wireOp",EDGE,"E111.1"),sQuery(id+"F19.wireOp",EDGE,"E111.3")])]})});
            var Q10;
            Q10=makeQuery(id+"F20.boolean.opBoolean","COPY",EDGE,{"derivedFrom":makeQuery(id+"F20.opExtrude","SWEPT_EDGE",EDGE,{"disambiguationData":[OSD([sQuery(id+"F19.wireOp",EDGE,"E111.3"),sQuery(id+"F19.wireOp",EDGE,"E111.4")])]})});
            var Q11;
            Q11=makeQuery(id+"F20.boolean.opBoolean","COPY",EDGE,{"derivedFrom":makeQuery(id+"F20.opExtrude","SWEPT_EDGE",EDGE,{"disambiguationData":[OSD([sQuery(id+"F19.wireOp",EDGE,"E111.4"),sQuery(id+"F19.wireOp",EDGE,"E117.trimOffspring")])]})});
            fillet(context, id + "F21", {"entities" : qUnion([Q0, Q1, Q2, Q3, Q4, Q5, Q6, Q7, Q8, Q9, Q10, Q11]), "radius" : 2 * mm, "tangentPropagation" : true, "allowEdgeOverflow" : false});
        }
    });
